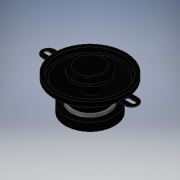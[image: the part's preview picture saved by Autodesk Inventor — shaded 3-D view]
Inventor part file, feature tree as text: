
AUTODESK INVENTOR PART (.ipt)
format: ipt  version: 2016 (Build 200138000, 138)  size: 230,912 bytes
history: native  units: mm
features: sketch x4, projected_geometry x3, extrude x2, revolve x2, mirror x1, fillet x1
ambient origin geometry x8: Origin, YZ Plane, XZ Plane, XY Plane, X Axis, Y Axis, Z Axis, Center Point
bodies: Solid1 (feature_tree)
feature tree (13):
  extrude  "Extrusion1"  Depth=78.0mm
  revolve  "Revolution1"  [1 undecoded]
  revolve  "Revolution2"  [1 undecoded]
  extrude  "Extrusion2"  Depth=3.0mm
  mirror  "Mirror1"
  fillet  "Fillet1"  Radius=7.0mm
  sketch  "Sketch1"  dims[d0=87.0mm d1=78.0mm]
  sketch  "Sketch2"  dims[d2=5.5mm d3=0.0mm d4=38.5mm]
  projected_geometry  "Projected Loop1"
  sketch  "Sketch3"  dims[d5=30.0mm d6=16.0mm]
  projected_geometry  "Projected Loop2"
  sketch  "Sketch4"  dims[d7=7.0mm d8=3.0mm d9=7.0mm d10=3.0mm d11=3.0mm d12=90.0deg d13=8.0mm d14=31.0mm d15=21.0mm d16=8.0mm d17=90.0deg d18=104.0mm d19=3.5mm d20=4.87mm d21=8.0mm d22=8.0mm d23=1.0mm d24=0.0mm d25=5.0mm]
  projected_geometry  "Projected Loop3"
note: 2 required parameter values undecoded (feature->parameter linkage not recoverable at this tier; creation-order binding heuristic only, values carry confidence <= 0.55)
